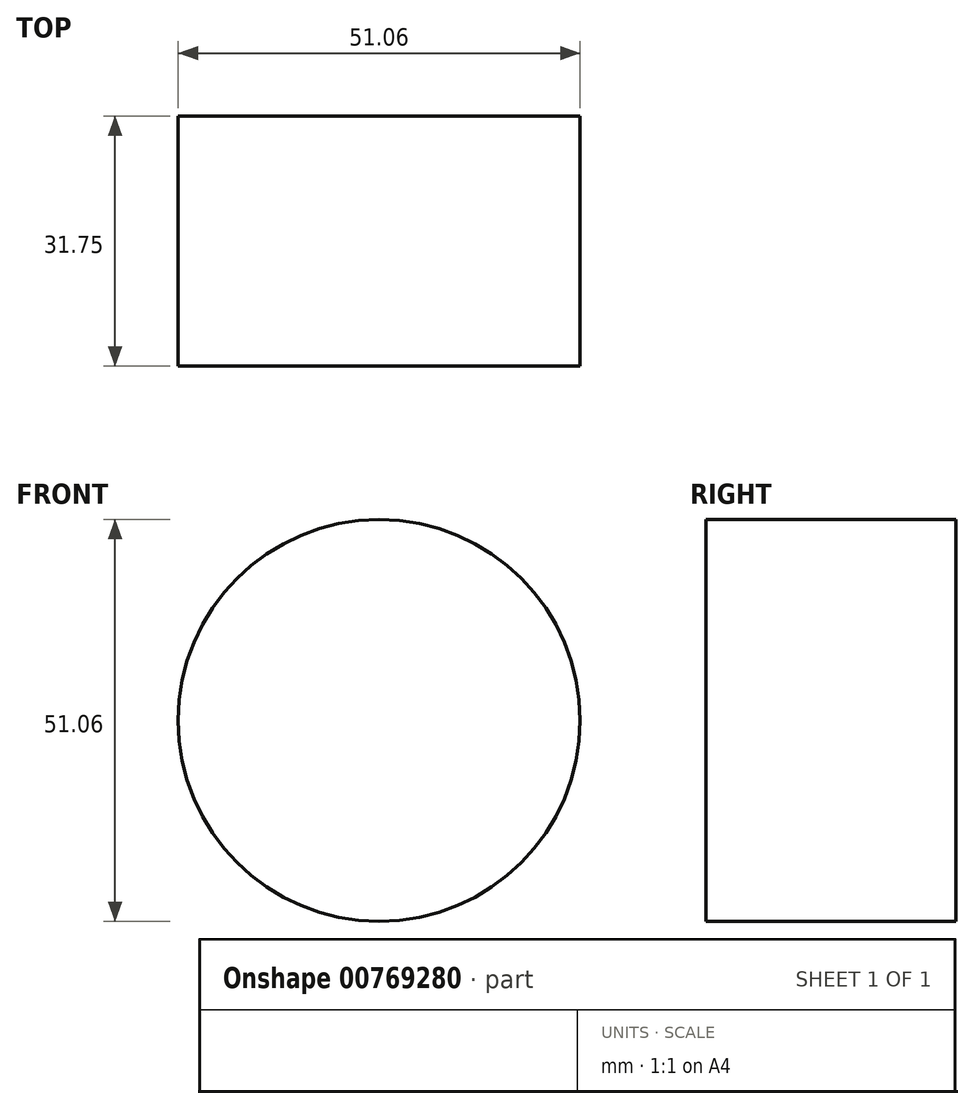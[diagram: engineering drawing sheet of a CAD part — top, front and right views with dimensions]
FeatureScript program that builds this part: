
annotation { "Feature Type Name" : "Feature", "Feature Type Description" : "" }
export const myFeature = defineFeature(function(context is Context, id is Id, definition is map)
    precondition{}
    {
        {
            var Q0;
            Q0=qCreatedBy(makeId("Front.planeOp"),FACE);
            var sketch = newSketch(context, id + "F0", { "sketchPlane" : qUnion([Q0])});
            skCircle(sketch, "E0", {"center": v(9.66, 31.2) * mm, "radius": 25.53 * mm});
            skSolve(sketch);
        }
        {
            var Q0;
            Q0=makeQuery(id+"F0.imprint","IMPRINT",FACE,{"disambiguationData":[TD([[makeQuery(id+"F0.imprint","IMPRINT",EDGE,{"derivedFrom":sQuery(id+"F0.wireOp",EDGE,"E0")}),1.0]])]});
            extrude(context, id + "F1", {"entities" : qUnion([Q0]), "depth" : 31.75 * mm, "offsetDistance" : 25.4 * mm});
        }
    });
